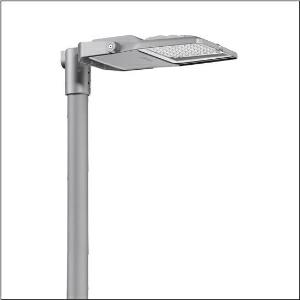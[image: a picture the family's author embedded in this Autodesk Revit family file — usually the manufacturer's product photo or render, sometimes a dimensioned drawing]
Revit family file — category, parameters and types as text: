
# Revit family: floodlight_fl_21_iq_mini___pl43_5xa7771c2a3a_69d2
name_source: partatom
category: Lighting Fixtures
units: mm (PartAtom-declared; Revit-internal decimal feet)

## family parameters
Cut with Voids When Loaded = No
Host = Face
Light Source = No
Part Type = Normal
Room Calculation Point = No
Round Connector Dimension = Use Diameter
Shared = No

## types (1)
- --- (1 x LED, 12520 lm, 87.2 W, 3000K)
    Apparent Load = 87 VA
    CIE Flux Codes = 27 78 99 100 100
    Color Rendering = 70
    Color Temperature = 3000K
    Default Elevation = 1800 mm
    Description = Floodlight FL 21 iQ mini, floodlight, primary light control with lens, of PMMA, primary optical cover: protective disc, of toughened safety glass, transparent, light distribution: PL43, light emission: direct distribution, installation type: surface-mounted, LED, High Power LED, rated luminous flux: 12.520lm, luminous efficacy: 144lm/W, light colour: 730, colour temperature: 3000K, control: Auto-Match, Temp-Guard, Lumen-Switch, Night-Set, Smart-Wire, Light-Fading, Desk-Remote (wireless, voltage-free reading and setting of iQ features in the workshop via application-optimized NFC function/RFID function), optimised constant luminous flux control (CLO 2.0), with terminal, 6-pole, mains connection: 220..240V, AC, 50/60Hz, start of lifetime: 87W, end of service life: 92W, reduction: 40W, luminaire housing, of diecast aluminium, powder-coated, Siteco® metallic grey (DB 702S), corrosivity category C5 mid according to DIN EN ISO 12944, sealing non-destructively replaceable, please order mast flange separately, mast bracket, of steel, galvanised, powder-coated, Siteco® metallic grey (DB 702S), protection rating (complete): IP66, insulation class (complete): insulation class II (safety insulation), certification: CE, ENEC, VDE, protection symbol: D, impact resistance: IK08, permissible operating ambient temperature: -40..+40°C, permissible operating ambient temperature for outdoor applications: -40..+50°C, standard: DIN EN 12944, LABS conformity tested according to VDMA 24364:2018-05, packaging unit: 1 piece

Light Distribution: PL43
    Height = 70 mm
    Lamp = 1 x LED
    Lamp Light Flux = 12520 lm
    Lamp Power = 87.2 W
    Lamp count = 1
    Length = 485 mm
    Luminous efficacy = 144 lm/W
    Manufacturer = Siteco
    ModVariant = No
    Model = 5XA7771C2A3A
    Number of Poles = 1
    OnlyDefault = Yes
    Power Factor = 1
    Product Name = Floodlight FL 21 iQ mini | PL43
    Product group = floodlight | pylon annexe
    ProductGroupID = 6200
    Protection Class = Protection class II
    Protection Degree = IP 66
    RLX_Detail_Level = 1
    RLX_Emergency_Light_Flux = 0 lm
    RLX_Emergency_Type = 0
    RLX_Emergency_Type_DB = No
    RlxData = <blob elided: 101229 chars, md5=06f3cd45>
    Socket = socket
    Standby Power = 0 W
    System Light Flux = 12520 lm
    System Power = 87 W
    Type Comments = factory setting: luminous flux: 100 % | dim-lin: 254 | 456 mA
    Type Image = l_1007125.jpg
    URL = http://relux.com
    VarID = @adj_112653
    Voltage = 0 V
    Weight = 0.00 kg
    Width = 337 mm

## geometry (parser evidence)
native form markers: Blend x4, Sweep x14
no freeform markers — native parametric forms only
